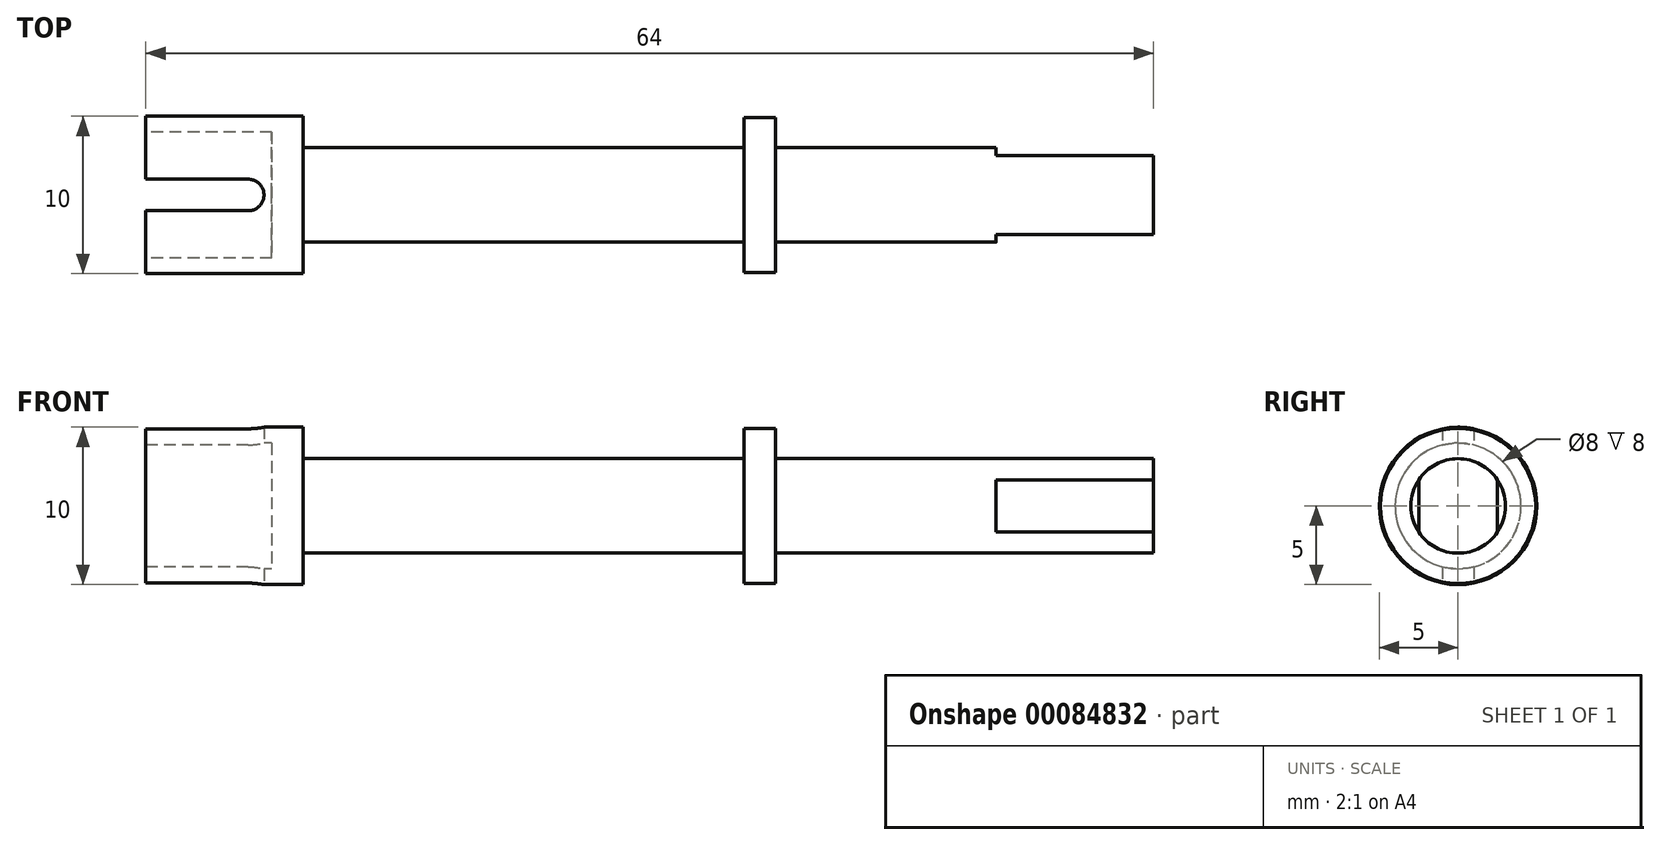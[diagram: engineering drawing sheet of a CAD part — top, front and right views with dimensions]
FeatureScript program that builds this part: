
annotation { "Feature Type Name" : "Feature", "Feature Type Description" : "" }
export const myFeature = defineFeature(function(context is Context, id is Id, definition is map)
    precondition{}
    {
        {
            var Q0;
            Q0=qCreatedBy(makeId("Right.planeOp"),FACE);
            var sketch = newSketch(context, id + "F0", { "sketchPlane" : qUnion([Q0])});
            skCircle(sketch, "E0", {"center": v(0, 0) * mm, "radius": 5 * mm});
            skSolve(sketch);
        }
        {
            var Q0;
            Q0 = qSketchRegion(id + "F0", true);
            extrude(context, id + "F1", {"entities" : qUnion([Q0]), "depth" : 64 * mm});
        }
        {
            var Q0;
            Q0=qCreatedBy(makeId("Front.planeOp"),FACE);
            var sketch = newSketch(context, id + "F2", { "sketchPlane" : qUnion([Q0])});
            skLineSegment(sketch, "E1", {"start": v(0, 0) * mm, "end": v(56.09, 0) * mm, "construction": true});
            skLineSegment(sketch, "E2.top", {"start": v(10, 3) * mm, "end": v(38, 3) * mm});
            skLineSegment(sketch, "E2.left", {"start": v(10, 6.42) * mm, "end": v(10, 3) * mm});
            skLineSegment(sketch, "E2.right", {"start": v(38, 4.93) * mm, "end": v(38, 3) * mm});
            skLineSegment(sketch, "E3", {"start": v(38, 4.93) * mm, "end": v(40, 4.93) * mm});
            skPoint(sketch, "E3.endSnap0", {"position": v(38, 4.93) * mm});
            skLineSegment(sketch, "E4", {"start": v(40, 4.93) * mm, "end": v(40, 3) * mm});
            skLineSegment(sketch, "E5", {"start": v(40, 3) * mm, "end": v(64, 3) * mm});
            skLineSegment(sketch, "E6", {"start": v(64, 3) * mm, "end": v(64, 6.42) * mm});
            skPoint(sketch, "E7.end.orphan", {"position": v(38, 6.86) * mm});
            skLineSegment(sketch, "E8", {"start": v(10, 6.42) * mm, "end": v(64, 6.42) * mm});
            skSolve(sketch);
        }
        {
            var Q0;
            Q0 = qSketchRegion(id + "F2", true);
            var Q1;
            Q1=sQuery(id+"F2.wireOp",EDGE,"E1");
            revolve(context, id + "F3", {"operationType" : NewBodyOperationType.REMOVE, "entities" : qUnion([Q0]), "axis" : qUnion([Q1]), "revolveType" : RevolveType.FULL, "oppositeDirection" : true});
        }
        {
            var Q0;
            Q0=makeQuery(id+"F1.opExtrude","CAP_FACE",FACE,{"disambiguationData":[OSD([sQuery(id+"F0.wireOp",EDGE,"E0")])],"isStart":false});
            var sketch = newSketch(context, id + "F4", { "sketchPlane" : qUnion([Q0])});
            skLineSegment(sketch, "E9.bottom", {"start": v(2.5, -7.12) * mm, "end": v(-2.5, -7.12) * mm});
            skLineSegment(sketch, "E9.top", {"start": v(2.5, 7.12) * mm, "end": v(-2.5, 7.12) * mm});
            skLineSegment(sketch, "E9.left", {"start": v(2.5, -7.12) * mm, "end": v(2.5, 7.12) * mm});
            skLineSegment(sketch, "E9.right", {"start": v(-2.5, -7.12) * mm, "end": v(-2.5, 7.12) * mm});
            skPoint(sketch, "E9.middle", {"position": v(0, 0) * mm});
            skLineSegment(sketch, "E10.bottom", {"start": v(9.48, -8.84) * mm, "end": v(-9.48, -8.84) * mm});
            skLineSegment(sketch, "E10.top", {"start": v(9.48, 8.84) * mm, "end": v(-9.48, 8.84) * mm});
            skLineSegment(sketch, "E10.left", {"start": v(9.48, -8.84) * mm, "end": v(9.48, 8.84) * mm});
            skLineSegment(sketch, "E10.right", {"start": v(-9.48, -8.84) * mm, "end": v(-9.48, 8.84) * mm});
            skSolve(sketch);
        }
        {
            var Q0;
            Q0 = qSketchRegion(id + "F4", true);
            extrude(context, id + "F5", {"entities" : qUnion([Q0]), "operationType" : NewBodyOperationType.REMOVE, "oppositeDirection" : true, "depth" : 10 * mm});
        }
        {
            var Q0;
            Q0=qCreatedBy(makeId("Top.planeOp"),FACE);
            var sketch = newSketch(context, id + "F6", { "sketchPlane" : qUnion([Q0])});
            skLineSegment(sketch, "E11.bottom", {"start": v(6.5, -1) * mm, "end": v(-6.5, -1) * mm});
            skLineSegment(sketch, "E11.top", {"start": v(6.5, 1) * mm, "end": v(-6.5, 1) * mm});
            skLineSegment(sketch, "E11.left", {"start": v(6.5, -1) * mm, "end": v(6.5, 1) * mm});
            skLineSegment(sketch, "E11.right", {"start": v(-6.5, -1) * mm, "end": v(-6.5, 1) * mm});
            skPoint(sketch, "E11.middle", {"position": v(0, 0) * mm});
            skArc(sketch, "E12", {"start": v(6.5, -1) * mm, "mid": v(7.5, 0) * mm, "end": v(6.5, 1) * mm});
            skSolve(sketch);
        }
        {
            var Q0;
            Q0 = qSketchRegion(id + "F6", true);
            extrude(context, id + "F7", {"entities" : qUnion([Q0]), "operationType" : NewBodyOperationType.REMOVE, "endBound" : BoundingType.SYMMETRIC, "depth" : 25 * mm});
        }
        {
            var Q0;
            {var subQ0=sQuery(id+"F0.wireOp",EDGE,"E0");Q0=makeQuery(id+"F7.boolean.opBoolean","SPLIT",FACE,{"disambiguationData":[TD([makeQuery(id+"F7.opExtrude","SWEPT_FACE",FACE,{"disambiguationData":[OSD([sQuery(id+"F6.wireOp",EDGE,"E11.top")])]})])],"derivedFrom":makeQuery(id+"F1.opExtrude","CAP_FACE",FACE,{"disambiguationData":[OSD([subQ0])],"isStart":true})});}
            var sketch = newSketch(context, id + "F8", { "sketchPlane" : qUnion([Q0])});
            skCircle(sketch, "E13", {"center": v(0, 0) * mm, "radius": 4 * mm});
            skSolve(sketch);
        }
        {
            var Q0;
            Q0 = qSketchRegion(id + "F8", true);
            extrude(context, id + "F9", {"entities" : qUnion([Q0]), "operationType" : NewBodyOperationType.REMOVE, "oppositeDirection" : true, "depth" : 8 * mm});
        }
    });
